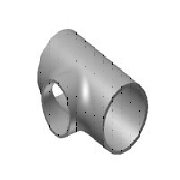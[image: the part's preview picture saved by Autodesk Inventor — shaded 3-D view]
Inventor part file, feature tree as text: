
AUTODESK INVENTOR PART (.ipt)
format: ipt  version: 2023.2 (Build 272271030, 271C)  size: 241,152 bytes
history: native  units: mm
features: other x6, extrude x4, sketch x4, fillet x2
ambient origin geometry x8: Origin, YZ Plane, XZ Plane, XY Plane, X Axis, Y Axis, Z Axis, Center Point
bodies: Solid1 (feature_tree)
feature tree (16):
  extrude  "Extrusion1"  Depth=260.0mm
  extrude  "Extrusion2"  Depth=108.0mm
  fillet  "Fillet1"  Radius=110.0mm
  extrude  "Extrusion3"  Depth=25.0mm
  extrude  "Extrusion4"  Depth=110.0mm
  fillet  "Fillet2"  [1 undecoded]
  other  "Work Point1"
  other  "Work Point2"
  other  "Work Point3"
  other  "Work Axis1"
  other  "Work Axis2"
  other  "Work Axis3"
  sketch  "Sketch1"  dims[d0=159.0mm d2=260.0mm]
  sketch  "Sketch2"  dims[d3=0.0mm d4=108.0mm d6=110.0mm]
  sketch  "Sketch3"  dims[d7=0.0mm d8=25.0mm]
  sketch  "Sketch4"  dims[d9=100.0mm d10=110.0mm d11=0.0mm d12=150.0mm d13=110.0mm d14=0.0mm d15=29.5mm]
note: 1 required parameter value undecoded (feature->parameter linkage not recoverable at this tier; creation-order binding heuristic only, values carry confidence <= 0.55)
